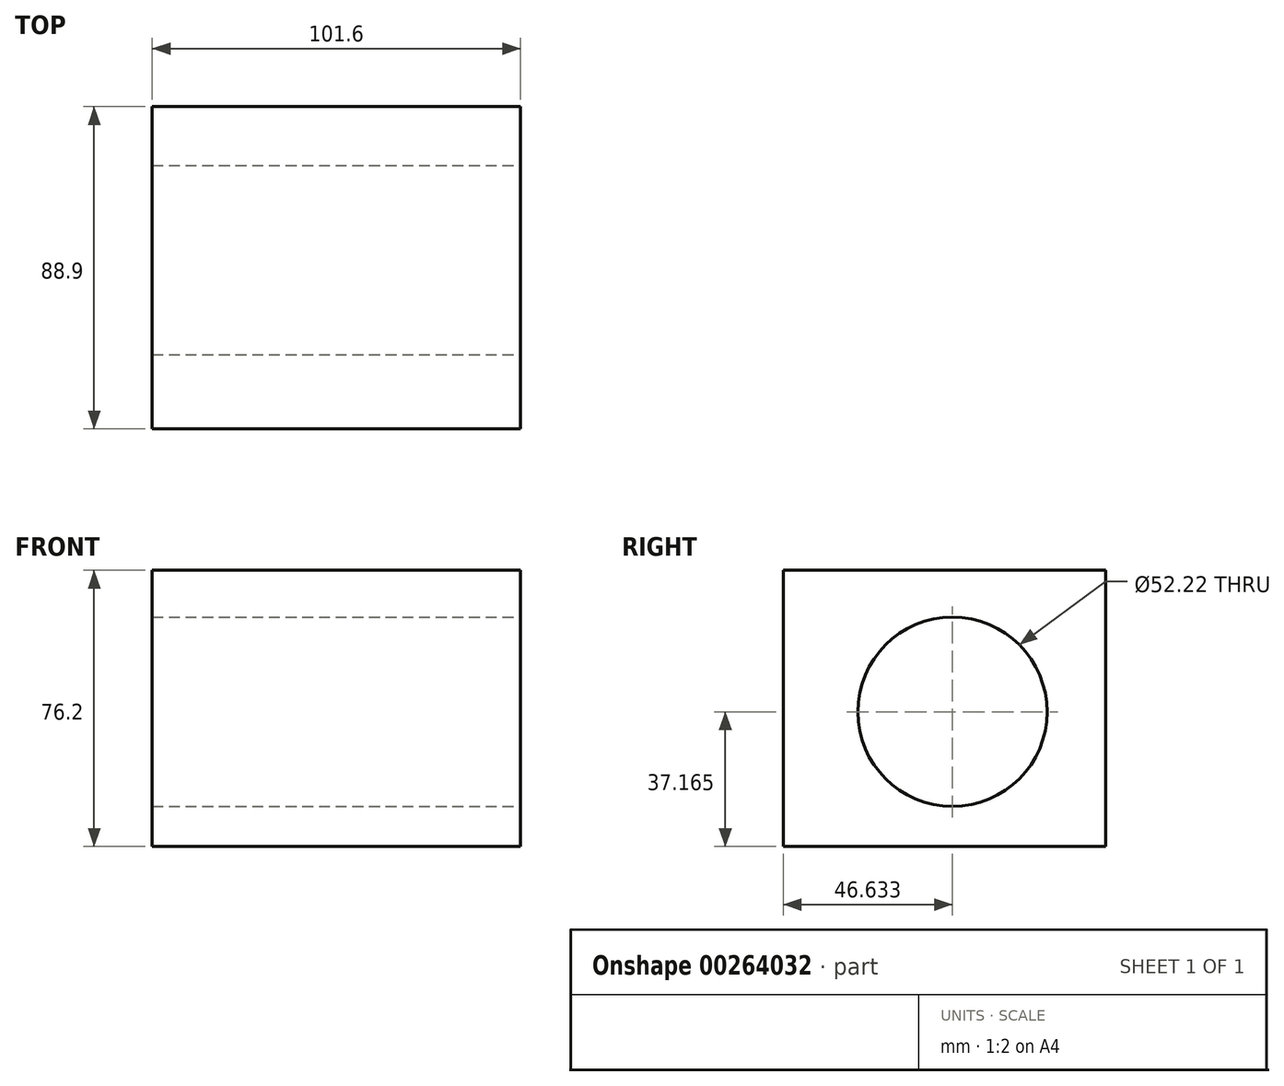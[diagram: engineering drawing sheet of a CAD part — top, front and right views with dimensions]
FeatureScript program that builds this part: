
annotation { "Feature Type Name" : "Feature", "Feature Type Description" : "" }
export const myFeature = defineFeature(function(context is Context, id is Id, definition is map)
    precondition{}
    {
        {
            var Q0;
            Q0=qCreatedBy(makeId("Front.planeOp"),FACE);
            var sketch = newSketch(context, id + "F0", { "sketchPlane" : qUnion([Q0])});
            skLineSegment(sketch, "E0.bottom", {"start": v(0, 0) * mm, "end": v(101.6, 0) * mm});
            skLineSegment(sketch, "E0.top", {"start": v(0, 76.2) * mm, "end": v(101.6, 76.2) * mm});
            skLineSegment(sketch, "E0.left", {"start": v(0, 0) * mm, "end": v(0, 76.2) * mm});
            skLineSegment(sketch, "E0.right", {"start": v(101.6, 0) * mm, "end": v(101.6, 76.2) * mm});
            skSolve(sketch);
        }
        {
            var Q0;
            Q0=makeQuery(id+"F0.imprint","IMPRINT",FACE,{"disambiguationData":[TD([[makeQuery(id+"F0.imprint","IMPRINT",EDGE,{"derivedFrom":sQuery(id+"F0.wireOp",EDGE,"E0.bottom")}),1.0]])]});
            extrude(context, id + "F1", {"entities" : qUnion([Q0]), "oppositeDirection" : true, "depth" : 50.8 * mm});
        }
        {
            var Q0;
            Q0=makeQuery(id+"F1.opExtrude","CAP_FACE",FACE,{"disambiguationData":[OSD([sQuery(id+"F0.wireOp",EDGE,"E0.bottom"),sQuery(id+"F0.wireOp",EDGE,"E0.top"),sQuery(id+"F0.wireOp",EDGE,"E0.left"),sQuery(id+"F0.wireOp",EDGE,"E0.right")])],"isStart":true});
            extrude(context, id + "F2", {"entities" : qUnion([Q0]), "operationType" : NewBodyOperationType.ADD, "depth" : 38.1 * mm});
        }
        {
            var Q0;
            {var subQ0=sQuery(id+"F0.wireOp",EDGE,"E0.right");Q0=makeQuery(id+"F2.boolean.opBoolean","MERGE",FACE,{"derivedFrom":[makeQuery(id+"F1.opExtrude","SWEPT_FACE",FACE,{"disambiguationData":[OSD([subQ0])]}),makeQuery(id+"F2.opExtrude","SWEPT_FACE",FACE,{"disambiguationData":[OSD([subQ0])]})]});}
            var sketch = newSketch(context, id + "F3", { "sketchPlane" : qUnion([Q0])});
            skCircle(sketch, "E1", {"center": v(8.53, 37.16) * mm, "radius": 26.1 * mm});
            skSolve(sketch);
        }
        {
            var Q0;
            Q0=makeQuery(id+"F3.imprint","IMPRINT",FACE,{"disambiguationData":[TD([[makeQuery(id+"F3.imprint","IMPRINT",EDGE,{"derivedFrom":sQuery(id+"F3.wireOp",EDGE,"E1")}),1.0]])]});
            extrude(context, id + "F4", {"entities" : qUnion([Q0]), "operationType" : NewBodyOperationType.REMOVE, "oppositeDirection" : true, "depth" : 101.6 * mm});
        }
    });
